FCSTD DOCUMENT  (FreeCAD 0.14R3703 (Git))
Label: arm
License: CC-BY 3.0
LicenseURL: http://creativecommons.org/licenses/by/3.0/
objects: Part::Part2DObjectPython×14
note: 14 computed .brp shape members not serialized (recipe doc carries the construction recipe); baked Part::Feature solids carry a one-line shape summary decoded from their .brp

FEATURE [Part::Part2DObjectPython] Circle003  # Draft 2D object (typed FeaturePython)
  FirstAngle = 0
  LastAngle = 0
  MakeFace = true
  Placement = pos=(10.5,95,0) rot=(0,0,1;0rad)
  Radius = 4
FEATURE [Part::Part2DObjectPython] Circle004  # Draft 2D object (typed FeaturePython)
  FirstAngle = 0
  LastAngle = 0
  MakeFace = true
  Placement = pos=(-10.5,95,0) rot=(0,0,1;0rad)
  Radius = 4
FEATURE [Part::Part2DObjectPython] Line  # Draft 2D object (typed FeaturePython)
  ChamferSize = 0
  Closed = false
  End = (10.5,99,0)
  FilletRadius = 0
  MakeFace = true
  Placement = pos=(0,-1,0) rot=(0,0,1;0rad)
  Points = (2) [(-10.5,100,0),(10.5,100,0)]
  Start = (-10.5,99,0)
FEATURE [Part::Part2DObjectPython] Line001  # Draft 2D object (typed FeaturePython)
  ChamferSize = 0
  Closed = false
  End = (-14.5,0,0)
  FilletRadius = 0
  MakeFace = true
  Points = (2) [(-14.5,95,0),(-14.5,0,0)]
  Start = (-14.5,95,0)
FEATURE [Part::Part2DObjectPython] Line002  # Draft 2D object (typed FeaturePython)
  ChamferSize = 0
  Closed = false
  End = (14.5,0,0)
  FilletRadius = 0
  MakeFace = true
  Points = (2) [(14.5,95,0),(14.5,0,0)]
  Start = (14.5,95,0)
FEATURE [Part::Part2DObjectPython] Circle  # Draft 2D object (typed FeaturePython)
  FirstAngle = 0
  LastAngle = 0
  MakeFace = true
  Radius = 20
FEATURE [Part::Part2DObjectPython] Circle002  # Draft 2D object (typed FeaturePython)
  FirstAngle = 0
  LastAngle = 0
  MakeFace = true
  Placement = pos=(10,85.5,0) rot=(0,0,1;0rad)
  Radius = 1.3
FEATURE [Part::Part2DObjectPython] Circle001  # Draft 2D object (typed FeaturePython)
  FirstAngle = 0
  LastAngle = 0
  MakeFace = true
  Placement = pos=(-10,95,0) rot=(0,0,1;0rad)
  Radius = 1.3
FEATURE [Part::Part2DObjectPython] Circle005  # Draft 2D object (typed FeaturePython)
  FirstAngle = 0
  LastAngle = 0
  MakeFace = true
  Placement = pos=(10,95,0) rot=(0,0,1;0rad)
  Radius = 1.3
FEATURE [Part::Part2DObjectPython] Circle006  # Draft 2D object (typed FeaturePython)
  FirstAngle = 0
  LastAngle = 0
  MakeFace = true
  Placement = pos=(-10.5,85.5,0) rot=(0,0,1;0rad)
  Radius = 1.3
FEATURE [Part::Part2DObjectPython] Circle007  # Draft 2D object (typed FeaturePython)
  FirstAngle = 0
  LastAngle = 0
  MakeFace = true
  Placement = pos=(5.6568,5.6568,0) rot=(0,0,1;0rad)
  Radius = 1.3
FEATURE [Part::Part2DObjectPython] Circle008  # Draft 2D object (typed FeaturePython)
  FirstAngle = 0
  LastAngle = 0
  MakeFace = true
  Placement = pos=(-5.6568,-5.6568,0) rot=(0,0,1;0rad)
  Radius = 1.3
FEATURE [Part::Part2DObjectPython] Circle009  # Draft 2D object (typed FeaturePython)
  FirstAngle = 0
  LastAngle = 0
  MakeFace = true
  Placement = pos=(6.7175,-6.7175,0) rot=(0,0,1;0rad)
  Radius = 1.3
FEATURE [Part::Part2DObjectPython] Circle010  # Draft 2D object (typed FeaturePython)
  FirstAngle = 0
  LastAngle = 0
  MakeFace = true
  Placement = pos=(-6.7175,6.7175,0) rot=(0,0,1;0rad)
  Radius = 1.3
